FCSTD DOCUMENT  (FreeCAD 0.20R29177 (Git))
Label: Bottom
License: All rights reserved
LicenseURL: http://en.wikipedia.org/wiki/All_rights_reserved
objects: Sketcher::SketchObject×1, PartDesign::Body×1
note: 2 computed .brp shape members not serialized (recipe doc carries the construction recipe); baked Part::Feature solids carry a one-line shape summary decoded from their .brp

FEATURE [Sketcher::SketchObject] Sketch
  FullyConstrained = true
  MapMode = 5
  Support = -> [XY_Plane]
  sketch-geometry (122):
    g0: LineSegment StartX=205 StartY=2e-16 StartZ=0 EndX=200 EndY=2e-16 EndZ=0
    g1: LineSegment StartX=200 StartY=2e-16 StartZ=0 EndX=200 EndY=3 EndZ=0
    g2: LineSegment StartX=200 StartY=3 StartZ=0 EndX=195 EndY=3 EndZ=0
    g3: LineSegment StartX=195 StartY=3 StartZ=0 EndX=195 EndY=0 EndZ=0
    g4: LineSegment StartX=195 StartY=0 StartZ=0 EndX=190 EndY=0 EndZ=0
    g5: LineSegment StartX=190 StartY=0 StartZ=0 EndX=190 EndY=3 EndZ=0
    g6: LineSegment StartX=190 StartY=3 StartZ=0 EndX=185 EndY=3 EndZ=0
    g7: LineSegment StartX=185 StartY=3 StartZ=0 EndX=185 EndY=0 EndZ=0
    g8: LineSegment StartX=185 StartY=0 StartZ=0 EndX=180 EndY=0 EndZ=0
    g9: LineSegment StartX=180 StartY=0 StartZ=0 EndX=180 EndY=3 EndZ=0
    g10: LineSegment StartX=180 StartY=3 StartZ=0 EndX=175 EndY=3 EndZ=0
    g11: LineSegment StartX=175 StartY=3 StartZ=0 EndX=175 EndY=0 EndZ=0
    g12: LineSegment StartX=175 StartY=0 StartZ=0 EndX=170 EndY=0 EndZ=0
    g13: LineSegment StartX=170 StartY=0 StartZ=0 EndX=170 EndY=3 EndZ=0
    g14: LineSegment StartX=170 StartY=3 StartZ=0 EndX=165 EndY=3 EndZ=0
    g15: LineSegment StartX=165 StartY=3 StartZ=0 EndX=165 EndY=0 EndZ=0
    g16: LineSegment StartX=165 StartY=0 StartZ=0 EndX=160 EndY=0 EndZ=0
    g17: LineSegment StartX=160 StartY=0 StartZ=0 EndX=160 EndY=3 EndZ=0
    g18: LineSegment StartX=160 StartY=3 StartZ=0 EndX=155 EndY=3 EndZ=0
    g19: LineSegment StartX=155 StartY=3 StartZ=0 EndX=155 EndY=0 EndZ=0
    g20: LineSegment StartX=155 StartY=0 StartZ=0 EndX=150 EndY=0 EndZ=0
    g21: LineSegment StartX=150 StartY=0 StartZ=0 EndX=150 EndY=3 EndZ=0
    g22: LineSegment StartX=150 StartY=3 StartZ=0 EndX=145 EndY=3 EndZ=0
    g23: LineSegment StartX=145 StartY=3 StartZ=0 EndX=145 EndY=0 EndZ=0
    g24: LineSegment StartX=145 StartY=0 StartZ=0 EndX=140 EndY=0 EndZ=0
    g25: LineSegment StartX=140 StartY=0 StartZ=0 EndX=140 EndY=3 EndZ=0
    g26: LineSegment StartX=140 StartY=3 StartZ=0 EndX=135 EndY=3 EndZ=0
    g27: LineSegment StartX=135 StartY=3 StartZ=0 EndX=135 EndY=0 EndZ=0
    g28: LineSegment StartX=135 StartY=0 StartZ=0 EndX=130 EndY=0 EndZ=0
    g29: LineSegment StartX=130 StartY=0 StartZ=0 EndX=130 EndY=3 EndZ=0
    g30: LineSegment StartX=130 StartY=3 StartZ=0 EndX=125 EndY=3 EndZ=0
    g31: LineSegment StartX=125 StartY=3 StartZ=0 EndX=125 EndY=0 EndZ=0
    g32: LineSegment StartX=125 StartY=0 StartZ=0 EndX=120 EndY=0 EndZ=0
    g33: LineSegment StartX=120 StartY=0 StartZ=0 EndX=120 EndY=3 EndZ=0
    g34: LineSegment StartX=120 StartY=3 StartZ=0 EndX=115 EndY=3 EndZ=0
    g35: LineSegment StartX=115 StartY=3 StartZ=0 EndX=115 EndY=0 EndZ=0
    g36: LineSegment StartX=115 StartY=0 StartZ=0 EndX=110 EndY=0 EndZ=0
    g37: LineSegment StartX=110 StartY=0 StartZ=0 EndX=110 EndY=3 EndZ=0
    g38: LineSegment StartX=110 StartY=3 StartZ=0 EndX=105 EndY=3 EndZ=0
    g39: LineSegment StartX=105 StartY=3 StartZ=0 EndX=105 EndY=0 EndZ=0
    g40: LineSegment StartX=105 StartY=0 StartZ=0 EndX=100 EndY=0 EndZ=0
    g41: LineSegment StartX=100 StartY=0 StartZ=0 EndX=100 EndY=3 EndZ=0
    g42: LineSegment StartX=100 StartY=3 StartZ=0 EndX=95 EndY=3 EndZ=0
    g43: LineSegment StartX=95 StartY=3 StartZ=0 EndX=95 EndY=0 EndZ=0
    g44: LineSegment StartX=95 StartY=0 StartZ=0 EndX=90 EndY=0 EndZ=0
    g45: LineSegment StartX=90 StartY=0 StartZ=0 EndX=90 EndY=3 EndZ=0
    g46: LineSegment StartX=90 StartY=3 StartZ=0 EndX=85 EndY=3 EndZ=0
    g47: LineSegment StartX=85 StartY=3 StartZ=0 EndX=85 EndY=0 EndZ=0
    g48: LineSegment StartX=85 StartY=0 StartZ=0 EndX=80 EndY=0 EndZ=0
    g49: LineSegment StartX=80 StartY=0 StartZ=0 EndX=80 EndY=3 EndZ=0
    g50: LineSegment StartX=80 StartY=3 StartZ=0 EndX=75 EndY=3 EndZ=0
    g51: LineSegment StartX=75 StartY=3 StartZ=0 EndX=75 EndY=0 EndZ=0
    g52: LineSegment StartX=75 StartY=0 StartZ=0 EndX=70 EndY=0 EndZ=0
    g53: LineSegment StartX=70 StartY=0 StartZ=0 EndX=70 EndY=3 EndZ=0
    g54: LineSegment StartX=70 StartY=3 StartZ=0 EndX=65 EndY=3 EndZ=0
    g55: LineSegment StartX=65 StartY=3 StartZ=0 EndX=65 EndY=0 EndZ=0
    g56: LineSegment StartX=65 StartY=0 StartZ=0 EndX=60 EndY=0 EndZ=0
    g57: LineSegment StartX=60 StartY=0 StartZ=0 EndX=60 EndY=3 EndZ=0
    g58: LineSegment StartX=60 StartY=3 StartZ=0 EndX=55 EndY=3 EndZ=0
    g59: LineSegment StartX=55 StartY=3 StartZ=0 EndX=55 EndY=0 EndZ=0
    g60: LineSegment StartX=55 StartY=0 StartZ=0 EndX=50 EndY=0 EndZ=0
    g61: LineSegment StartX=50 StartY=0 StartZ=0 EndX=50 EndY=3 EndZ=0
    g62: LineSegment StartX=50 StartY=3 StartZ=0 EndX=45 EndY=3 EndZ=0
    g63: LineSegment StartX=45 StartY=3 StartZ=0 EndX=45 EndY=0 EndZ=0
    g64: LineSegment StartX=45 StartY=0 StartZ=0 EndX=40 EndY=0 EndZ=0
    g65: LineSegment StartX=40 StartY=0 StartZ=0 EndX=40 EndY=3 EndZ=0
    g66: LineSegment StartX=40 StartY=3 StartZ=0 EndX=35 EndY=3 EndZ=0
    g67: LineSegment StartX=35 StartY=3 StartZ=0 EndX=35 EndY=0 EndZ=0
    g68: LineSegment StartX=35 StartY=0 StartZ=0 EndX=30 EndY=0 EndZ=0
    g69: LineSegment StartX=30 StartY=0 StartZ=0 EndX=30 EndY=3 EndZ=0
    g70: LineSegment StartX=30 StartY=3 StartZ=0 EndX=25 EndY=3 EndZ=0
    g71: LineSegment StartX=25 StartY=3 StartZ=0 EndX=25 EndY=0 EndZ=0
    g72: LineSegment StartX=25 StartY=0 StartZ=0 EndX=20 EndY=0 EndZ=0
    g73: LineSegment StartX=20 StartY=0 StartZ=0 EndX=20 EndY=3 EndZ=0
    g74: LineSegment StartX=20 StartY=3 StartZ=0 EndX=15 EndY=3 EndZ=0
    g75: LineSegment StartX=15 StartY=3 StartZ=0 EndX=15 EndY=0 EndZ=0
    g76: LineSegment StartX=15 StartY=0 StartZ=0 EndX=10 EndY=0 EndZ=0
    g77: LineSegment StartX=10 StartY=0 StartZ=0 EndX=10 EndY=3 EndZ=0
    g78: LineSegment StartX=10 StartY=3 StartZ=0 EndX=5 EndY=3 EndZ=0
    g79: LineSegment StartX=5 StartY=3 StartZ=0 EndX=5 EndY=0 EndZ=0
    g80: LineSegment StartX=5 StartY=0 StartZ=0 EndX=0 EndY=0 EndZ=0
    g81: LineSegment StartX=205 StartY=2e-16 StartZ=0 EndX=205 EndY=5 EndZ=0
    g82: LineSegment StartX=205 StartY=5 StartZ=0 EndX=208 EndY=5 EndZ=0
    g83: LineSegment StartX=208 StartY=5 StartZ=0 EndX=208 EndY=9 EndZ=0
    g84: LineSegment StartX=208 StartY=9 StartZ=0 EndX=205 EndY=9 EndZ=0
    g85: LineSegment StartX=205 StartY=9 StartZ=0 EndX=205 EndY=13 EndZ=0
    g86: LineSegment StartX=205 StartY=13 StartZ=0 EndX=208 EndY=13 EndZ=0
    g87: LineSegment StartX=208 StartY=13 StartZ=0 EndX=208 EndY=17 EndZ=0
    g88: LineSegment StartX=208 StartY=17 StartZ=0 EndX=205 EndY=17 EndZ=0
    g89: LineSegment StartX=205 StartY=17 StartZ=0 EndX=205 EndY=21 EndZ=0
    g90: LineSegment StartX=205 StartY=21 StartZ=0 EndX=208 EndY=21 EndZ=0
    g91: LineSegment StartX=208 StartY=21 StartZ=0 EndX=208 EndY=25 EndZ=0
    g92: LineSegment StartX=208 StartY=25 StartZ=0 EndX=205 EndY=25 EndZ=0
    g93: LineSegment StartX=205 StartY=25 StartZ=0 EndX=205 EndY=29 EndZ=0
    g94: LineSegment StartX=205 StartY=29 StartZ=0 EndX=208 EndY=29 EndZ=0
    g95: LineSegment StartX=208 StartY=29 StartZ=0 EndX=208 EndY=33 EndZ=0
    g96: LineSegment StartX=208 StartY=33 StartZ=0 EndX=205 EndY=33 EndZ=0
    g97: LineSegment StartX=205 StartY=33 StartZ=0 EndX=205 EndY=37 EndZ=0
    g98: LineSegment StartX=205 StartY=37 StartZ=0 EndX=208 EndY=37 EndZ=0
    g99: LineSegment StartX=208 StartY=37 StartZ=0 EndX=208 EndY=41 EndZ=0
    g100: LineSegment StartX=208 StartY=41 StartZ=0 EndX=205 EndY=41 EndZ=0
    g101: LineSegment StartX=205 StartY=41 StartZ=0 EndX=205 EndY=45 EndZ=0
    g102: LineSegment StartX=205 StartY=45 StartZ=0 EndX=208 EndY=45 EndZ=0
    g103: LineSegment StartX=208 StartY=45 StartZ=0 EndX=208 EndY=49 EndZ=0
    g104: LineSegment StartX=208 StartY=49 StartZ=0 EndX=205 EndY=49 EndZ=0
    g105: LineSegment StartX=205 StartY=49 StartZ=0 EndX=205 EndY=53 EndZ=0
    g106: LineSegment StartX=205 StartY=53 StartZ=0 EndX=208 EndY=53 EndZ=0
    g107: LineSegment StartX=208 StartY=53 StartZ=0 EndX=208 EndY=57 EndZ=0
    g108: LineSegment StartX=208 StartY=57 StartZ=0 EndX=205 EndY=57 EndZ=0
    g109: LineSegment StartX=205 StartY=57 StartZ=0 EndX=205 EndY=61 EndZ=0
    g110: LineSegment StartX=205 StartY=61 StartZ=0 EndX=208 EndY=61 EndZ=0
    g111: LineSegment StartX=208 StartY=61 StartZ=0 EndX=208 EndY=65 EndZ=0
    g112: LineSegment StartX=208 StartY=65 StartZ=0 EndX=205 EndY=65 EndZ=0
    g113: LineSegment StartX=205 StartY=65 StartZ=0 EndX=205 EndY=69 EndZ=0
    g114: LineSegment StartX=205 StartY=69 StartZ=0 EndX=208 EndY=69 EndZ=0
    g115: LineSegment StartX=208 StartY=69 StartZ=0 EndX=208 EndY=73 EndZ=0
    g116: LineSegment StartX=208 StartY=73 StartZ=0 EndX=205 EndY=73 EndZ=0
    g117: LineSegment StartX=205 StartY=73 StartZ=0 EndX=205 EndY=77 EndZ=0
    g118: LineSegment StartX=205 StartY=77 StartZ=0 EndX=208 EndY=77 EndZ=0
    g119: LineSegment StartX=208 StartY=77 StartZ=0 EndX=208 EndY=81 EndZ=0
    g120: LineSegment StartX=208 StartY=81 StartZ=0 EndX=205 EndY=81 EndZ=0
    g121: LineSegment StartX=205 StartY=81 StartZ=0 EndX=205 EndY=86 EndZ=0
  constraints (366):
    c: Horizontal(g0)
    c: Coincident(g0,g1)
    c: Vertical(g1)
    c: Coincident(g1,g2)
    c: Coincident(g2,g3)
    c: Coincident(g3,g4)
    c: Horizontal(g4)
    c: Coincident(g4,g5)
    c: Coincident(g5,g6)
    c: Coincident(g6,g7)
    c: Vertical(g7)
    c: Coincident(g7,g8)
    c: Horizontal(g8)
    c: Coincident(g8,g9)
    c: Vertical(g9)
    c: Coincident(g9,g10)
    c: Horizontal(g10)
    c: Coincident(g10,g11)
    c: Vertical(g11)
    c: Coincident(g11,g12)
    c: Coincident(g12,g13)
    c: Vertical(g13)
    c: Coincident(g13,g14)
    c: Coincident(g14,g15)
    c: Coincident(g15,g16)
    c: Coincident(g16,g17)
    c: Coincident(g17,g18)
    c: Horizontal(g18)
    c: Coincident(g18,g19)
    c: Coincident(g19,g20)
    c: Coincident(g20,g21)
    c: Coincident(g21,g22)
    c: Coincident(g22,g23)
    c: Vertical(g23)
    c: Coincident(g23,g24)
    c: Coincident(g24,g25)
    c: Vertical(g25)
    c: Coincident(g25,g26)
    c: Horizontal(g26)
    c: Coincident(g26,g27)
    c: Vertical(g27)
    c: Coincident(g27,g28)
    c: Horizontal(g28)
    c: Coincident(g28,g29)
    c: Coincident(g29,g30)
    c: Horizontal(g30)
    c: Coincident(g30,g31)
    c: Coincident(g31,g32)
    c: Horizontal(g32)
    c: Coincident(g32,g33)
    c: Vertical(g33)
    c: Coincident(g33,g34)
    c: Horizontal(g34)
    c: Coincident(g34,g35)
    c: Vertical(g35)
    c: Coincident(g35,g36)
    c: Horizontal(g36)
    c: Coincident(g36,g37)
    c: Vertical(g37)
    c: Coincident(g37,g38)
    c: Coincident(g38,g39)
    c: Vertical(g39)
    c: Coincident(g39,g40)
    c: Coincident(g40,g41)
    c: Coincident(g41,g42)
    c: Horizontal(g42)
    c: Coincident(g42,g43)
    c: Coincident(g43,g44)
    c: Horizontal(g44)
    c: Coincident(g44,g45)
    c: Vertical(g45)
    c: Coincident(g45,g46)
    c: Coincident(g46,g47)
    c: Coincident(g47,g48)
    c: Horizontal(g48)
    c: Coincident(g48,g49)
    c: Vertical(g49)
    c: Coincident(g49,g50)
    c: Horizontal(g50)
    c: Coincident(g50,g51)
    c: Coincident(g51,g52)
    c: Horizontal(g52)
    c: Coincident(g52,g53)
    c: Coincident(g53,g54)
    c: Coincident(g54,g55)
    c: Vertical(g55)
    c: Coincident(g55,g56)
    c: Horizontal(g56)
    c: Coincident(g56,g57)
    c: Vertical(g57)
    c: Coincident(g57,g58)
    c: Horizontal(g58)
    c: Coincident(g58,g59)
    c: Coincident(g59,g60)
    c: Coincident(g60,g61)
    c: Coincident(g61,g62)
    c: Coincident(g62,g63)
    c: Coincident(g63,g64)
    c: Horizontal(g64)
    c: Coincident(g64,g65)
    c: Vertical(g65)
    c: Coincident(g65,g66)
    c: Coincident(g66,g67)
    c: Coincident(g67,g68)
    c: Horizontal(g68)
    c: Coincident(g68,g69)
    c: Coincident(g69,g70)
    c: Horizontal(g70)
    c: Coincident(g70,g71)
    c: Coincident(g71,g72)
    c: Horizontal(g72)
    c: Coincident(g72,g73)
    c: Vertical(g73)
    c: Coincident(g73,g74)
    c: Horizontal(g74)
    c: Coincident(g74,g75)
    c: Coincident(g75,g76)
    c: Coincident(g76,g77)
    c: Coincident(g77,g78)
    c: Horizontal(g78)
    c: Coincident(g78,g79)
    c: Vertical(g79)
    c: Coincident(g79,g80)
    c: Equal(g0,g80)
    c: Equal(g78,g76)
    c: Equal(g76,g74)
    c: Equal(g74,g72)
    c: Equal(g72,g70)
    c: Equal(g70,g68)
    c: Equal(g68,g66)
    c: Equal(g66,g64)
    c: Equal(g64,g62)
    c: Equal(g62,g60)
    c: Equal(g60,g58)
    c: Equal(g58,g56)
    c: Equal(g56,g54)
    c: Equal(g54,g52)
    c: Equal(g52,g50)
    c: Equal(g50,g48)
    c: Equal(g48,g46)
    c: Equal(g46,g44)
    c: Equal(g44,g42)
    c: Equal(g42,g40)
    c: Equal(g40,g38)
    c: Equal(g38,g36)
    c: Equal(g36,g34)
    c: Equal(g34,g32)
    c: Equal(g32,g30)
    c: Equal(g30,g28)
    c: Equal(g28,g26)
    c: Equal(g26,g24)
    c: Equal(g24,g22)
    c: Equal(g22,g20)
    c: Equal(g20,g18)
    c: Equal(g18,g16)
    c: Equal(g16,g14)
    c: Equal(g14,g12)
    c: Equal(g12,g10)
    c: Equal(g10,g8)
    c: Equal(g8,g6)
    c: Equal(g6,g4)
    c: Equal(g4,g2)
    c: Horizontal(g80)
    c: Vertical(g77)
    c: Vertical(g75)
    c: Horizontal(g76)
    c: Horizontal(g60)
    c: Vertical(g71)
    c: Vertical(g69)
    c: Vertical(g67)
    c: Vertical(g63)
    c: Vertical(g61)
    c: Vertical(g59)
    c: Horizontal(g66)
    c: Horizontal(g62)
    c: Horizontal(g46)
    c: Horizontal(g38)
    c: Horizontal(g40)
    c: Vertical(g53)
    c: Vertical(g51)
    c: Vertical(g47)
    c: Vertical(g43)
    c: Vertical(g41)
    c: Horizontal(g54)
    c: Horizontal(g22)
    c: Horizontal(g14)
    c: Vertical(g31)
    c: Vertical(g29)
    c: Vertical(g21)
    c: Vertical(g19)
    c: Vertical(g15)
    c: Vertical(g17)
    c: Horizontal(g24)
    c: Horizontal(g20)
    c: Horizontal(g16)
    c: Horizontal(g12)
    c: Horizontal(g6)
    c: Horizontal(g2)
    c: Vertical(g5)
    c: Vertical(g3)
    c: Equal(g79,g77)
    c: Equal(g77,g75)
    c: Equal(g75,g73)
    c: Equal(g73,g71)
    c: Equal(g71,g69)
    c: Equal(g69,g67)
    c: Equal(g67,g65)
    c: Equal(g65,g63)
    c: Equal(g63,g61)
    c: Equal(g61,g59)
    c: Equal(g59,g57)
    c: Equal(g57,g55)
    c: Equal(g55,g53)
    c: Equal(g53,g51)
    c: Equal(g51,g49)
    c: Equal(g49,g47)
    c: Equal(g47,g45)
    c: Equal(g45,g43)
    c: Equal(g43,g41)
    c: Equal(g41,g39)
    c: Equal(g39,g37)
    c: Equal(g37,g35)
    c: Equal(g35,g33)
    c: Equal(g33,g31)
    c: Equal(g31,g29)
    c: Equal(g29,g27)
    c: Equal(g27,g25)
    c: Equal(g25,g23)
    c: Equal(g23,g21)
    c: Equal(g21,g19)
    c: Equal(g19,g17)
    c: Equal(g17,g15)
    c: Equal(g15,g13)
    c: Equal(g13,g11)
    c: Equal(g11,g9)
    c: Equal(g9,g7)
    c: Equal(g7,g5)
    c: Equal(g5,g3)
    c: Equal(g3,g1)
    c: DistanceY(g1,g1) = 3
    c: DistanceX(g2,g2) = 5
    c: DistanceX(g0,g0) = 5
    c: Coincident(g80,g-1)
    c: Vertical(g81)
    c: Coincident(g81,g82)
    c: Coincident(g82,g83)
    c: Vertical(g83)
    c: Coincident(g83,g84)
    c: Horizontal(g84)
    c: Coincident(g84,g85)
    c: Vertical(g85)
    c: Coincident(g85,g86)
    c: Coincident(g86,g87)
    c: Vertical(g87)
    c: Coincident(g87,g88)
    c: Horizontal(g88)
    c: Coincident(g88,g89)
    c: Coincident(g89,g90)
    c: Horizontal(g90)
    c: Coincident(g90,g91)
    c: Coincident(g91,g92)
    c: Horizontal(g92)
    c: Coincident(g92,g93)
    c: Coincident(g93,g94)
    c: Horizontal(g94)
    c: Coincident(g94,g95)
    c: Coincident(g95,g96)
    c: Horizontal(g96)
    c: Coincident(g96,g97)
    c: Coincident(g97,g98)
    c: Horizontal(g98)
    c: Coincident(g98,g99)
    c: Coincident(g99,g100)
    c: Horizontal(g100)
    c: Coincident(g100,g101)
    c: Coincident(g101,g102)
    c: Coincident(g102,g103)
    c: Coincident(g103,g104)
    c: Coincident(g104,g105)
    c: Vertical(g105)
    c: Coincident(g105,g106)
    c: Coincident(g106,g107)
    c: Vertical(g107)
    c: Coincident(g107,g108)
    c: Horizontal(g108)
    c: Coincident(g108,g109)
    c: Coincident(g109,g110)
    c: Horizontal(g110)
    c: Coincident(g110,g111)
    c: Coincident(g111,g112)
    c: Coincident(g112,g113)
    c: Vertical(g113)
    c: Coincident(g113,g114)
    c: Horizontal(g114)
    c: Coincident(g114,g115)
    c: Vertical(g115)
    c: Coincident(g115,g116)
    c: Horizontal(g116)
    c: Coincident(g116,g117)
    c: Vertical(g117)
    c: Coincident(g117,g118)
    c: Horizontal(g118)
    c: Coincident(g118,g119)
    c: Vertical(g119)
    c: Coincident(g119,g120)
    c: Coincident(g120,g121)
    c: Vertical(g109)
    c: Vertical(g101)
    c: Vertical(g99)
    c: Vertical(g93)
    c: Vertical(g89)
    c: Vertical(g91)
    c: Vertical(g111)
    c: Equal(g121,g81)
    c: Horizontal(g120)
    c: Horizontal(g112)
    c: Horizontal(g106)
    c: Horizontal(g102)
    c: Horizontal(g82)
    c: Vertical(g95)
    c: Vertical(g97)
    c: Vertical(g103)
    c: Horizontal(g104)
    c: Horizontal(g86)
    c: Vertical(g121)
    c: Equal(g119,g117)
    c: Equal(g117,g115)
    c: Equal(g115,g113)
    c: Equal(g113,g111)
    c: Equal(g111,g109)
    c: Equal(g109,g107)
    c: Equal(g107,g105)
    c: Equal(g105,g103)
    c: Equal(g103,g101)
    c: Equal(g101,g99)
    c: Equal(g99,g97)
    c: Equal(g97,g95)
    c: Equal(g95,g93)
    c: Equal(g93,g91)
    c: Equal(g91,g89)
    c: Equal(g89,g87)
    c: Equal(g87,g85)
    c: Equal(g85,g83)
    c: Equal(g120,g118)
    c: Equal(g118,g116)
    c: Equal(g116,g114)
    c: Equal(g114,g112)
    c: Equal(g112,g110)
    c: Equal(g110,g108)
    c: Equal(g108,g106)
    c: Equal(g106,g104)
    c: Equal(g104,g102)
    c: Equal(g102,g100)
    c: Equal(g100,g98)
    c: Equal(g98,g96)
    c: Equal(g96,g94)
    c: Equal(g94,g92)
    c: Equal(g92,g90)
    c: Equal(g90,g88)
    c: Equal(g88,g86)
    c: Equal(g86,g84)
    c: Equal(g84,g82)
    c: DistanceX(g82,g82) = 3
    c: DistanceY(g83,g83) = 4
    c: DistanceY(g81,g81) = 5
    c: Coincident(g0,g81)
FEATURE [PartDesign::Body] Body
  Group = -> [Sketch]
  Origin = -> Origin
